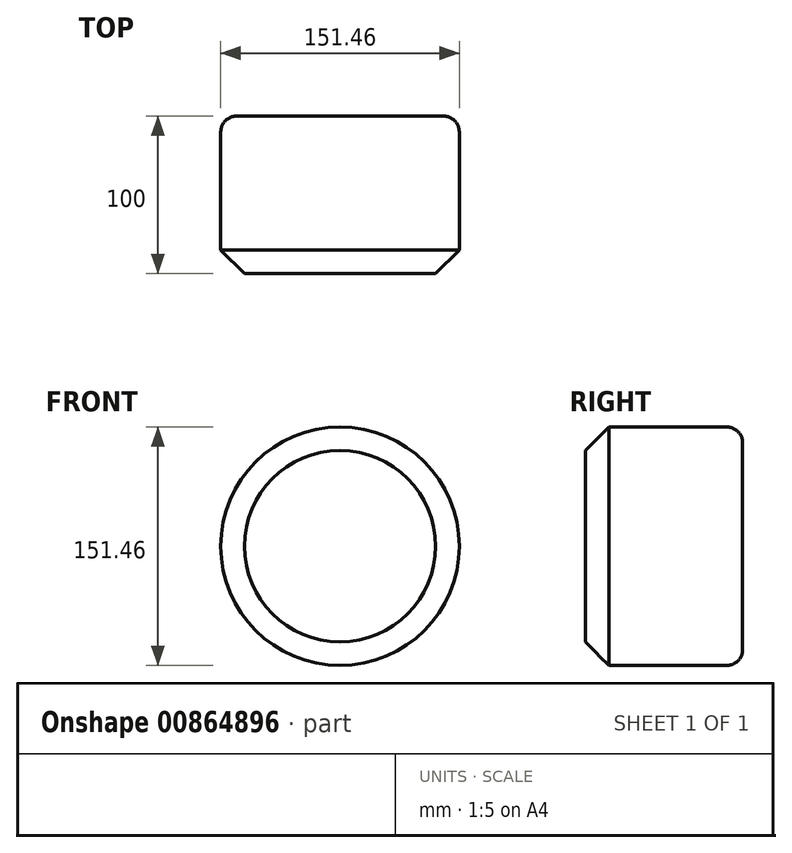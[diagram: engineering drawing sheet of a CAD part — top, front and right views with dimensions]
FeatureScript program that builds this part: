
annotation { "Feature Type Name" : "Feature", "Feature Type Description" : "" }
export const myFeature = defineFeature(function(context is Context, id is Id, definition is map)
    precondition{}
    {
        {
            var Q0;
            Q0=qCreatedBy(makeId("Front.planeOp"),FACE);
            var sketch = newSketch(context, id + "F0", { "sketchPlane" : qUnion([Q0])});
            skCircle(sketch, "E0", {"center": v(0, 0) * mm, "radius": 75.73 * mm});
            skSolve(sketch);
        }
        {
            var Q0;
            Q0 = qSketchRegion(id + "F0", true);
            var sketch = newSketch(context, id + "F1", { "sketchPlane" : qUnion([Q0])});
            skSolve(sketch);
        }
        {
            var Q0;
            Q0=makeQuery(id+"F1.imprint","IMPRINT",FACE,{"disambiguationData":[TD([[makeQuery(id+"F1.imprint","IMPRINT",EDGE,{"derivedFrom":makeQuery(id+"F0.imprint","IMPRINT",EDGE,{"derivedFrom":sQuery(id+"F0.wireOp",EDGE,"E0")})}),1.0]])]});
            extrude(context, id + "F2", {"entities" : qUnion([Q0]), "depth" : 100 * mm, "offsetDistance" : 25 * mm});
        }
        {
            var Q0;
            Q0=makeQuery(id+"F2.opExtrude","CAP_EDGE",EDGE,{"disambiguationData":[OSD([sQuery(id+"F0.wireOp",EDGE,"E0")])],"isStart":true});
            fillet(context, id + "F3", {"entities" : qUnion([Q0]), "radius" : 10 * mm, "tangentPropagation" : true, "allowEdgeOverflow" : false});
        }
        {
            var Q0;
            Q0=makeQuery(id+"F2.opExtrude","CAP_EDGE",EDGE,{"disambiguationData":[OSD([sQuery(id+"F0.wireOp",EDGE,"E0")])],"isStart":false});
            chamfer(context, id + "F4", {"entities" : qUnion([Q0]), "width" : 15 * mm, "tangentPropagation" : true});
        }
    });
